# Revit family: Automatic Barrier-Ditec-Qik7EH
name_source: partatom
category: Electrical Fixtures
revit_build: Autodesk Revit Architecture 2014 (Build: 20130308_1515(x64)
units: mm (PartAtom-declared; Revit-internal decimal feet)

## types (1)
- Automatic Barrier-Ditec-Qik7EH
    Arm Length = 3000 mm  [stored 9.84252 ft]
    Arm Length Constraint = 3000 mm  [stored 9.84252 ft]
    Barrier Mounting Base = Yes
    Barrier Mounting Base back lines = No
    Closing speed = 2÷6 s/90°
    Control panel = EL31R + M1QK (built-in)
    Design country = Italy
    Duty class = 5 - heavy duty
    Edition number = 1
    Installation instructions = http://ftp.ditec.it
    Intermittent operation = S2 = 60 min, S3 = 60%
    Manufacturer country = China
    Manufacturer name = Ditec
    Material main = Steel
    Material secondary = Plastic
    Nominal height = 1050
    Nominal width = 300
    Opening speed = 2÷6 s/90°
    Operating temperature = -20°C / +55°C  (-35°C / +55°C with NIO enabled), (-10°C / +50°C with battery)
    Power input = 1 A
    Power supply = 230 V AC / 50-60 Hz
    Product Guid = 776337cf-841a-4556-9f4e-64578078620e
    Product SKU = dit-qik7
    Product data url = http://bimobject.com
    Product dimensions (mm) = 300x320x1050
    Product family = Gate Automation & Barriers
    Product group = Automatic Barriers
    Protection rating = IP 24D
    QR code = http://bimobject.com
    Release for manual opening = Key-operated
    Stroke control = encoder
    Torque/Thrust = 70 Nm
    Weight Net (Kg) = 0

note: [stored X ft] marks values corroborated as IEEE doubles in the binary element streams (Revit-internal decimal feet)

## geometry (parser evidence)
native form markers: Blend x2, Sweep x10
no freeform markers — native parametric forms only
